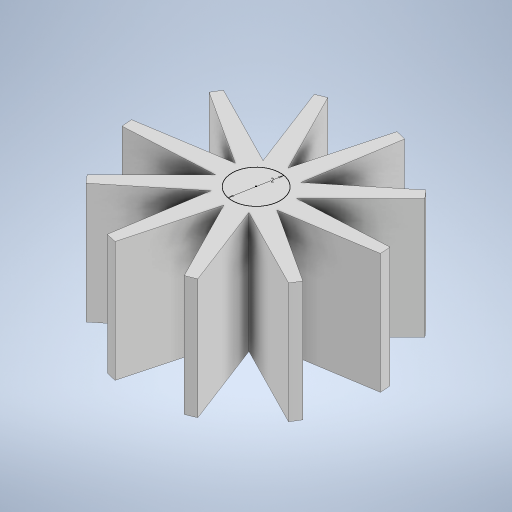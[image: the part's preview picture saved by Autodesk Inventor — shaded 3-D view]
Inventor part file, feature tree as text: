
AUTODESK INVENTOR PART (.ipt)
format: ipt  version: 2024 (Build 280153000, 153)  size: 260,608 bytes
history: native  units: mm
features: sketch x2, extrude x1
ambient origin geometry x8: Origin, YZ Plane, XZ Plane, XY Plane, X Axis, Y Axis, Z Axis, Center Point
bodies: Solid1 (feature_tree)
feature tree (3):
  extrude  "Extrusion1"  Depth=10.0mm TaperAngle=360.0deg
  sketch  "Sketch2"  dims[d5=5.0mm d6=0.0mm d7=2.0mm]
  sketch  "Sketch1"  dims[d0=10.0mm d1=100.0mm d3=360.0deg]
